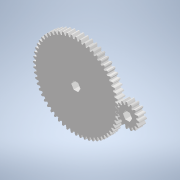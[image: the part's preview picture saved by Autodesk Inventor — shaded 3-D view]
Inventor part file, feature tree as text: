
AUTODESK INVENTOR PART (.ipt)
format: ipt  version: 2022 (Build 260153000, 153)  size: 4,653,568 bytes
history: native  units: mm
features: extrude x4, sketch x2
ambient origin geometry x8: Origin, YZ Plane, XZ Plane, XY Plane, X Axis, Y Axis, Z Axis, Center Point
bodies: Solid1 (feature_tree)
feature tree (6):
  sketch  "Sketch1"  dims[d0=5.55mm d1=0.0mm d2=5.55mm d3=0.0mm]
  extrude  "Extrusion1"  Depth=5.55mm TaperAngle=0.0deg
  extrude  "Extrusion2"  Depth=60.0mm TaperAngle=360.0deg
  sketch  "Sketch2"  dims[d4=3.0mm d5=60.0mm d7=360.0deg d9=3.0mm d10=60.0mm d12=360.0deg d14=0.3mm d15=0.3mm d16=6.0mm d17=0.0mm d18=6.0mm d19=0.0mm]
  extrude  "Extrusion3"  Depth=3.0mm
  extrude  "Extrusion4"  Depth=60.0mm TaperAngle=360.0deg
